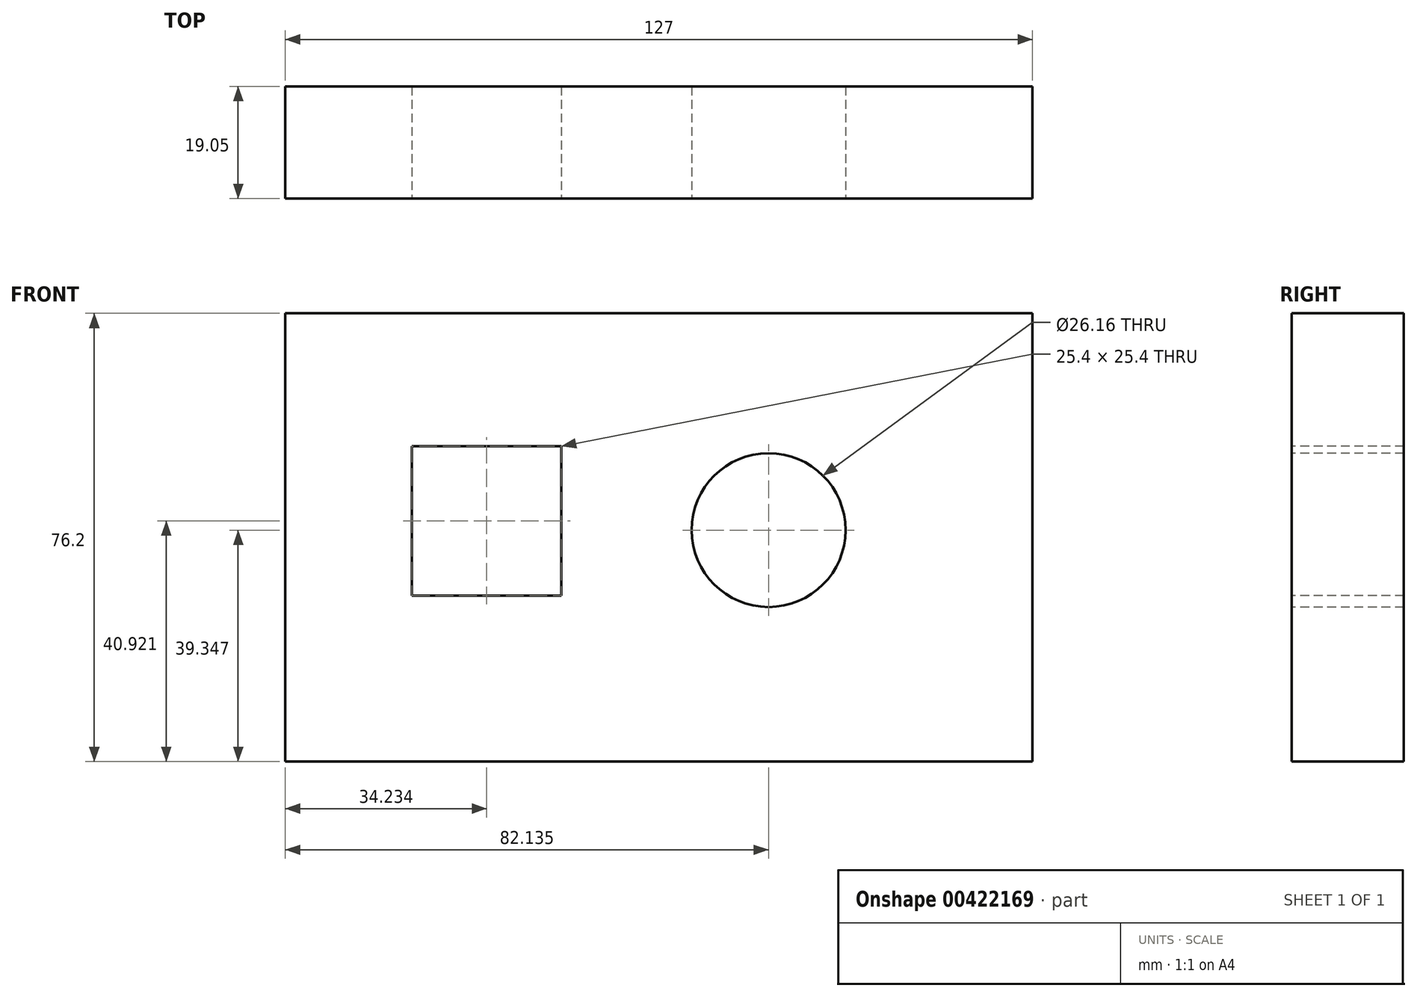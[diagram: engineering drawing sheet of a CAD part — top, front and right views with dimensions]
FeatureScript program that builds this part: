
annotation { "Feature Type Name" : "Feature", "Feature Type Description" : "" }
export const myFeature = defineFeature(function(context is Context, id is Id, definition is map)
    precondition{}
    {
        {
            var Q0;
            Q0=qCreatedBy(makeId("Front.planeOp"),FACE);
            var sketch = newSketch(context, id + "F0", { "sketchPlane" : qUnion([Q0])});
            skLineSegment(sketch, "E0", {"start": v(-75.56, 0) * mm, "end": v(51.44, 0) * mm});
            skLineSegment(sketch, "E1", {"start": v(51.44, 0) * mm, "end": v(51.44, 76.2) * mm});
            skLineSegment(sketch, "E2", {"start": v(51.44, 76.2) * mm, "end": v(-75.56, 76.2) * mm});
            skLineSegment(sketch, "E3", {"start": v(-75.56, 76.2) * mm, "end": v(-75.56, 0) * mm});
            skSolve(sketch);
        }
        {
            var Q0;
            Q0 = qSketchRegion(id + "F0", true);
            extrude(context, id + "F1", {"entities" : qUnion([Q0]), "depth" : 19.05 * mm});
        }
        {
            var Q0;
            Q0=makeQuery(id+"F1.opExtrude","CAP_FACE",FACE,{"disambiguationData":[OSD([sQuery(id+"F0.wireOp",EDGE,"E0"),sQuery(id+"F0.wireOp",EDGE,"E1"),sQuery(id+"F0.wireOp",EDGE,"E2"),sQuery(id+"F0.wireOp",EDGE,"E3")])],"isStart":false});
            var sketch = newSketch(context, id + "F2", { "sketchPlane" : qUnion([Q0])});
            skLineSegment(sketch, "E4.bottom", {"start": v(-54.03, 53.62) * mm, "end": v(-28.63, 53.62) * mm});
            skLineSegment(sketch, "E4.top", {"start": v(-54.03, 28.22) * mm, "end": v(-28.63, 28.22) * mm});
            skLineSegment(sketch, "E4.left", {"start": v(-54.03, 53.62) * mm, "end": v(-54.03, 28.22) * mm});
            skLineSegment(sketch, "E4.right", {"start": v(-28.63, 53.62) * mm, "end": v(-28.63, 28.22) * mm});
            skCircle(sketch, "E5", {"center": v(6.57, 39.35) * mm, "radius": 13.08 * mm});
            skSolve(sketch);
        }
        {
            var Q0;
            Q0=makeQuery(id+"F2.imprint","IMPRINT",FACE,{"disambiguationData":[TD([[makeQuery(id+"F2.imprint","IMPRINT",EDGE,{"derivedFrom":sQuery(id+"F2.wireOp",EDGE,"E5")}),1.0]])]});
            var Q1;
            Q1=makeQuery(id+"F2.imprint","IMPRINT",FACE,{"disambiguationData":[TD([[makeQuery(id+"F2.imprint","IMPRINT",EDGE,{"derivedFrom":sQuery(id+"F2.wireOp",EDGE,"E4.bottom")}),-1.0]])]});
            extrude(context, id + "F3", {"entities" : qUnion([Q0, Q1]), "operationType" : NewBodyOperationType.REMOVE, "oppositeDirection" : true, "depth" : 2540 * mm});
        }
    });
